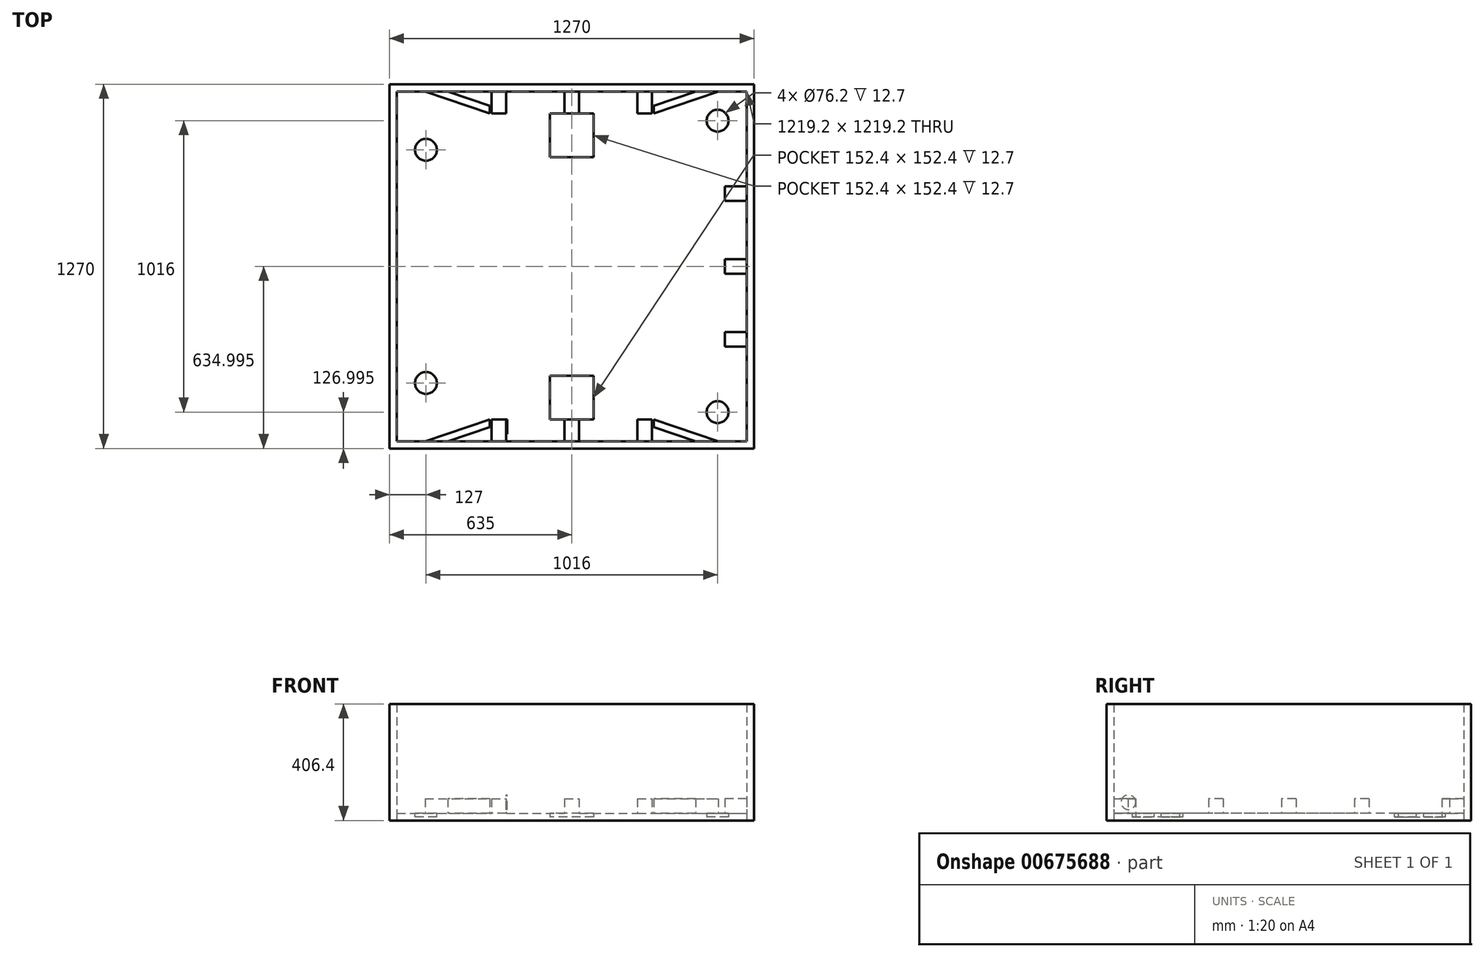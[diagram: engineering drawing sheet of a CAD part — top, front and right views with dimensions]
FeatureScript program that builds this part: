
annotation { "Feature Type Name" : "Feature", "Feature Type Description" : "" }
export const myFeature = defineFeature(function(context is Context, id is Id, definition is map)
    precondition{}
    {
        {
            var Q0;
            Q0=qCreatedBy(makeId("Top.planeOp"),FACE);
            var sketch = newSketch(context, id + "F0", { "sketchPlane" : qUnion([Q0])});
            skLineSegment(sketch, "E0.bottom", {"start": v(-620.85, 787.77) * mm, "end": v(598.35, 787.77) * mm});
            skLineSegment(sketch, "E0.top", {"start": v(-620.85, -431.43) * mm, "end": v(598.35, -431.43) * mm});
            skLineSegment(sketch, "E0.left", {"start": v(-620.85, 787.77) * mm, "end": v(-620.85, -431.43) * mm});
            skLineSegment(sketch, "E0.right", {"start": v(598.35, 787.77) * mm, "end": v(598.35, -431.43) * mm});
            skSolve(sketch);
        }
        {
            var Q0;
            Q0=makeQuery(id+"F0.imprint","IMPRINT",FACE,{"disambiguationData":[TD([[makeQuery(id+"F0.imprint","IMPRINT",EDGE,{"derivedFrom":sQuery(id+"F0.wireOp",EDGE,"E0.bottom")}),-1.0]])]});
            extrude(context, id + "F1", {"entities" : qUnion([Q0]), "depth" : 25.4 * mm, "offsetDistance" : 25.4 * mm});
        }
        {
            var Q0;
            Q0=makeQuery(id+"F1.opExtrude","CAP_FACE",FACE,{"disambiguationData":[OSD([sQuery(id+"F0.wireOp",EDGE,"E0.bottom"),sQuery(id+"F0.wireOp",EDGE,"E0.top"),sQuery(id+"F0.wireOp",EDGE,"E0.left"),sQuery(id+"F0.wireOp",EDGE,"E0.right")])],"isStart":false});
            var sketch = newSketch(context, id + "F2", { "sketchPlane" : qUnion([Q0])});
            skLineSegment(sketch, "E1", {"start": v(-36.65, -431.43) * mm, "end": v(-36.65, -355.23) * mm});
            skLineSegment(sketch, "E2", {"start": v(-36.65, -355.23) * mm, "end": v(14.15, -355.23) * mm});
            skLineSegment(sketch, "E3", {"start": v(14.15, -355.23) * mm, "end": v(14.15, -431.43) * mm});
            skLineSegment(sketch, "E4", {"start": v(14.15, -431.43) * mm, "end": v(-36.65, -431.43) * mm});
            skLineSegment(sketch, "E5.bottom", {"start": v(-239.85, -431.43) * mm, "end": v(-290.65, -431.43) * mm});
            skLineSegment(sketch, "E5.top", {"start": v(-239.85, -355.23) * mm, "end": v(-290.65, -355.23) * mm});
            skLineSegment(sketch, "E5.left", {"start": v(-239.85, -431.43) * mm, "end": v(-239.85, -355.23) * mm});
            skLineSegment(sketch, "E5.right", {"start": v(-290.65, -431.43) * mm, "end": v(-290.65, -355.23) * mm});
            skLineSegment(sketch, "E6.bottom", {"start": v(217.35, -431.43) * mm, "end": v(268.15, -431.43) * mm});
            skLineSegment(sketch, "E6.top", {"start": v(217.35, -355.23) * mm, "end": v(268.15, -355.23) * mm});
            skLineSegment(sketch, "E6.left", {"start": v(217.35, -431.43) * mm, "end": v(217.35, -355.23) * mm});
            skLineSegment(sketch, "E6.right", {"start": v(268.15, -431.43) * mm, "end": v(268.15, -355.23) * mm});
            skLineSegment(sketch, "E7.bottom", {"start": v(-239.85, 787.77) * mm, "end": v(-290.65, 787.77) * mm});
            skLineSegment(sketch, "E7.top", {"start": v(-239.85, 711.57) * mm, "end": v(-290.65, 711.57) * mm});
            skLineSegment(sketch, "E7.left", {"start": v(-239.85, 787.77) * mm, "end": v(-239.85, 711.57) * mm});
            skLineSegment(sketch, "E7.right", {"start": v(-290.65, 787.77) * mm, "end": v(-290.65, 711.57) * mm});
            skLineSegment(sketch, "E8.bottom", {"start": v(14.15, 787.77) * mm, "end": v(-36.65, 787.77) * mm});
            skLineSegment(sketch, "E8.top", {"start": v(14.15, 711.57) * mm, "end": v(-36.65, 711.57) * mm});
            skLineSegment(sketch, "E8.left", {"start": v(14.15, 787.77) * mm, "end": v(14.15, 711.57) * mm});
            skLineSegment(sketch, "E8.right", {"start": v(-36.65, 787.77) * mm, "end": v(-36.65, 711.57) * mm});
            skLineSegment(sketch, "E9.bottom", {"start": v(217.35, 787.77) * mm, "end": v(268.15, 787.77) * mm});
            skLineSegment(sketch, "E9.top", {"start": v(217.35, 711.57) * mm, "end": v(268.15, 711.57) * mm});
            skLineSegment(sketch, "E9.left", {"start": v(217.35, 787.77) * mm, "end": v(217.35, 711.57) * mm});
            skLineSegment(sketch, "E9.right", {"start": v(268.15, 787.77) * mm, "end": v(268.15, 711.57) * mm});
            skSolve(sketch);
        }
        {
            var Q0;
            Q0=makeQuery(id+"F2.imprint","IMPRINT",FACE,{"disambiguationData":[TD([[makeQuery(id+"F2.imprint","IMPRINT",EDGE,{"derivedFrom":sQuery(id+"F2.wireOp",EDGE,"E7.bottom")}),-1.0]])]});
            var Q1;
            Q1=makeQuery(id+"F2.imprint","IMPRINT",FACE,{"disambiguationData":[TD([[makeQuery(id+"F2.imprint","IMPRINT",EDGE,{"derivedFrom":sQuery(id+"F2.wireOp",EDGE,"E8.bottom")}),-1.0]])]});
            var Q2;
            Q2=makeQuery(id+"F2.imprint","IMPRINT",FACE,{"disambiguationData":[TD([[makeQuery(id+"F2.imprint","IMPRINT",EDGE,{"derivedFrom":sQuery(id+"F2.wireOp",EDGE,"E9.bottom")}),-1.0]])]});
            var Q3;
            Q3=makeQuery(id+"F2.imprint","IMPRINT",FACE,{"disambiguationData":[TD([[makeQuery(id+"F2.imprint","IMPRINT",EDGE,{"derivedFrom":sQuery(id+"F2.wireOp",EDGE,"E5.bottom")}),1.0]])]});
            var Q4;
            Q4=makeQuery(id+"F2.imprint","IMPRINT",FACE,{"disambiguationData":[TD([[makeQuery(id+"F2.imprint","IMPRINT",EDGE,{"derivedFrom":sQuery(id+"F2.wireOp",EDGE,"E1")}),-1.0]])]});
            var Q5;
            Q5=makeQuery(id+"F2.imprint","IMPRINT",FACE,{"disambiguationData":[TD([[makeQuery(id+"F2.imprint","IMPRINT",EDGE,{"derivedFrom":sQuery(id+"F2.wireOp",EDGE,"E6.bottom")}),1.0]])]});
            extrude(context, id + "F3", {"entities" : qUnion([Q0, Q1, Q2, Q3, Q4, Q5]), "operationType" : NewBodyOperationType.ADD, "depth" : 50.8 * mm, "offsetDistance" : 25.4 * mm});
        }
        {
            var Q0;
            Q0=makeQuery(id+"F1.opExtrude","CAP_FACE",FACE,{"disambiguationData":[OSD([sQuery(id+"F0.wireOp",EDGE,"E0.bottom"),sQuery(id+"F0.wireOp",EDGE,"E0.top"),sQuery(id+"F0.wireOp",EDGE,"E0.left"),sQuery(id+"F0.wireOp",EDGE,"E0.right")])],"isStart":false});
            var sketch = newSketch(context, id + "F4", { "sketchPlane" : qUnion([Q0])});
            skLineSegment(sketch, "E10", {"start": v(274.5, -355.23) * mm, "end": v(499.84, -431.43) * mm});
            skLineSegment(sketch, "E11", {"start": v(499.84, -431.43) * mm, "end": v(420.55, -431.43) * mm});
            skLineSegment(sketch, "E12", {"start": v(420.55, -431.43) * mm, "end": v(274.5, -382.05) * mm});
            skLineSegment(sketch, "E13", {"start": v(274.5, -382.05) * mm, "end": v(274.5, -355.23) * mm});
            skLineSegment(sketch, "E14", {"start": v(-522.34, -431.43) * mm, "end": v(-297, -355.23) * mm});
            skLineSegment(sketch, "E15", {"start": v(-297, -355.23) * mm, "end": v(-297, -382.05) * mm});
            skLineSegment(sketch, "E16", {"start": v(-297, -382.05) * mm, "end": v(-443.05, -431.43) * mm});
            skLineSegment(sketch, "E17", {"start": v(-443.05, -431.43) * mm, "end": v(-522.34, -431.43) * mm});
            skLineSegment(sketch, "E18", {"start": v(-522.34, 787.77) * mm, "end": v(-297, 711.57) * mm});
            skLineSegment(sketch, "E19", {"start": v(-297, 711.57) * mm, "end": v(-297, 738.38) * mm});
            skLineSegment(sketch, "E20", {"start": v(-297, 738.38) * mm, "end": v(-443.05, 787.77) * mm});
            skLineSegment(sketch, "E21", {"start": v(-443.05, 787.77) * mm, "end": v(-522.34, 787.77) * mm});
            skLineSegment(sketch, "E22", {"start": v(420.55, 787.77) * mm, "end": v(274.5, 738.38) * mm});
            skLineSegment(sketch, "E23", {"start": v(274.5, 738.38) * mm, "end": v(274.5, 711.57) * mm});
            skLineSegment(sketch, "E24", {"start": v(274.5, 711.57) * mm, "end": v(499.84, 787.77) * mm});
            skLineSegment(sketch, "E25", {"start": v(499.84, 787.77) * mm, "end": v(420.55, 787.77) * mm});
            skSolve(sketch);
        }
        {
            var Q0;
            Q0=makeQuery(id+"F4.imprint","IMPRINT",FACE,{"disambiguationData":[TD([[makeQuery(id+"F4.imprint","IMPRINT",EDGE,{"derivedFrom":sQuery(id+"F4.wireOp",EDGE,"E18")}),1.0]])]});
            var Q1;
            Q1=makeQuery(id+"F4.imprint","IMPRINT",FACE,{"disambiguationData":[TD([[makeQuery(id+"F4.imprint","IMPRINT",EDGE,{"derivedFrom":sQuery(id+"F4.wireOp",EDGE,"E22")}),1.0]])]});
            var Q2;
            Q2=makeQuery(id+"F4.imprint","IMPRINT",FACE,{"disambiguationData":[TD([[makeQuery(id+"F4.imprint","IMPRINT",EDGE,{"derivedFrom":sQuery(id+"F4.wireOp",EDGE,"E10")}),-1.0]])]});
            var Q3;
            Q3=makeQuery(id+"F4.imprint","IMPRINT",FACE,{"disambiguationData":[TD([[makeQuery(id+"F4.imprint","IMPRINT",EDGE,{"derivedFrom":sQuery(id+"F4.wireOp",EDGE,"E14")}),-1.0]])]});
            extrude(context, id + "F5", {"entities" : qUnion([Q0, Q1, Q2, Q3]), "depth" : 50.8 * mm, "offsetDistance" : 25.4 * mm});
        }
        {
            var Q0;
            Q0=makeQuery(id+"F1.opExtrude","CAP_FACE",FACE,{"disambiguationData":[OSD([sQuery(id+"F0.wireOp",EDGE,"E0.bottom"),sQuery(id+"F0.wireOp",EDGE,"E0.top"),sQuery(id+"F0.wireOp",EDGE,"E0.left"),sQuery(id+"F0.wireOp",EDGE,"E0.right")])],"isStart":false});
            var sketch = newSketch(context, id + "F6", { "sketchPlane" : qUnion([Q0])});
            skLineSegment(sketch, "E26.bottom", {"start": v(598.35, 203.57) * mm, "end": v(522.15, 203.57) * mm});
            skLineSegment(sketch, "E26.top", {"start": v(598.35, 152.77) * mm, "end": v(522.15, 152.77) * mm});
            skLineSegment(sketch, "E26.left", {"start": v(598.35, 203.57) * mm, "end": v(598.35, 152.77) * mm});
            skLineSegment(sketch, "E26.right", {"start": v(522.15, 203.57) * mm, "end": v(522.15, 152.77) * mm});
            skLineSegment(sketch, "E27.bottom", {"start": v(598.35, 457.57) * mm, "end": v(522.15, 457.57) * mm});
            skLineSegment(sketch, "E27.top", {"start": v(598.35, 406.77) * mm, "end": v(522.15, 406.77) * mm});
            skLineSegment(sketch, "E27.left", {"start": v(598.35, 457.57) * mm, "end": v(598.35, 406.77) * mm});
            skLineSegment(sketch, "E27.right", {"start": v(522.15, 457.57) * mm, "end": v(522.15, 406.77) * mm});
            skLineSegment(sketch, "E28.bottom", {"start": v(522.15, -50.43) * mm, "end": v(598.35, -50.43) * mm});
            skLineSegment(sketch, "E28.top", {"start": v(522.15, -101.23) * mm, "end": v(598.35, -101.23) * mm});
            skLineSegment(sketch, "E28.left", {"start": v(522.15, -50.43) * mm, "end": v(522.15, -101.23) * mm});
            skLineSegment(sketch, "E28.right", {"start": v(598.35, -50.43) * mm, "end": v(598.35, -101.23) * mm});
            skSolve(sketch);
        }
        {
            var Q0;
            Q0=makeQuery(id+"F6.imprint","IMPRINT",FACE,{"disambiguationData":[TD([[makeQuery(id+"F6.imprint","IMPRINT",EDGE,{"derivedFrom":sQuery(id+"F6.wireOp",EDGE,"E27.bottom")}),1.0]])]});
            var Q1;
            Q1=makeQuery(id+"F6.imprint","IMPRINT",FACE,{"disambiguationData":[TD([[makeQuery(id+"F6.imprint","IMPRINT",EDGE,{"derivedFrom":sQuery(id+"F6.wireOp",EDGE,"E26.bottom")}),1.0]])]});
            var Q2;
            Q2=makeQuery(id+"F6.imprint","IMPRINT",FACE,{"disambiguationData":[TD([[makeQuery(id+"F6.imprint","IMPRINT",EDGE,{"derivedFrom":sQuery(id+"F6.wireOp",EDGE,"E28.bottom")}),-1.0]])]});
            extrude(context, id + "F7", {"entities" : qUnion([Q0, Q1, Q2]), "operationType" : NewBodyOperationType.ADD, "depth" : 50.8 * mm, "offsetDistance" : 25.4 * mm});
        }
        {
            var Q0;
            Q0=makeQuery(id+"F1.opExtrude","CAP_FACE",FACE,{"disambiguationData":[OSD([sQuery(id+"F0.wireOp",EDGE,"E0.bottom"),sQuery(id+"F0.wireOp",EDGE,"E0.top"),sQuery(id+"F0.wireOp",EDGE,"E0.left"),sQuery(id+"F0.wireOp",EDGE,"E0.right")])],"isStart":true});
            var sketch = newSketch(context, id + "F8", { "sketchPlane" : qUnion([Q0])});
            skLineSegment(sketch, "E29", {"start": v(-620.85, 431.43) * mm, "end": v(-620.85, -787.77) * mm});
            skLineSegment(sketch, "E30", {"start": v(-620.85, -787.77) * mm, "end": v(598.35, -787.77) * mm});
            skLineSegment(sketch, "E31", {"start": v(598.35, -787.77) * mm, "end": v(598.35, 431.43) * mm});
            skLineSegment(sketch, "E32", {"start": v(598.35, 431.43) * mm, "end": v(-620.85, 431.43) * mm});
            skLineSegment(sketch, "E33", {"start": v(-671.65, 482.23) * mm, "end": v(-671.65, -838.57) * mm});
            skLineSegment(sketch, "E34", {"start": v(-671.65, -838.57) * mm, "end": v(649.15, -838.57) * mm});
            skLineSegment(sketch, "E35", {"start": v(649.15, -838.57) * mm, "end": v(649.15, 482.23) * mm});
            skLineSegment(sketch, "E36", {"start": v(649.15, 482.23) * mm, "end": v(-671.65, 482.23) * mm});
            skSolve(sketch);
        }
        {
            var Q0;
            Q0=makeQuery(id+"F8.imprint","IMPRINT",FACE,{"disambiguationData":[TD([[makeQuery(id+"F8.imprint","IMPRINT",EDGE,{"derivedFrom":sQuery(id+"F8.wireOp",EDGE,"E29")}),1.0]])]});
            extrude(context, id + "F9", {"entities" : qUnion([Q0]), "oppositeDirection" : true, "depth" : 609.6 * mm, "offsetDistance" : 25.4 * mm});
        }
        {
            var Q0;
            Q0=makeQuery(id+"F9.opExtrude","SWEPT_FACE",FACE,{"disambiguationData":[OSD([sQuery(id+"F8.wireOp",EDGE,"E34")])]});
            extrude(context, id + "F10", {"entities" : qUnion([Q0]), "operationType" : NewBodyOperationType.REMOVE, "oppositeDirection" : true, "depth" : 25.4 * mm, "offsetDistance" : 25.4 * mm});
        }
        {
            var Q0;
            Q0=makeQuery(id+"F9.opExtrude","SWEPT_FACE",FACE,{"disambiguationData":[OSD([sQuery(id+"F8.wireOp",EDGE,"E33")])]});
            extrude(context, id + "F11", {"entities" : qUnion([Q0]), "operationType" : NewBodyOperationType.REMOVE, "oppositeDirection" : true, "depth" : 25.4 * mm, "offsetDistance" : 25.4 * mm});
        }
        {
            var Q0;
            Q0=makeQuery(id+"F9.opExtrude","SWEPT_FACE",FACE,{"disambiguationData":[OSD([sQuery(id+"F8.wireOp",EDGE,"E36")])]});
            extrude(context, id + "F12", {"entities" : qUnion([Q0]), "operationType" : NewBodyOperationType.REMOVE, "oppositeDirection" : true, "depth" : 25.4 * mm, "offsetDistance" : 25.4 * mm});
        }
        {
            var Q0;
            Q0=makeQuery(id+"F9.opExtrude","SWEPT_FACE",FACE,{"disambiguationData":[OSD([sQuery(id+"F8.wireOp",EDGE,"E35")])]});
            extrude(context, id + "F13", {"entities" : qUnion([Q0]), "operationType" : NewBodyOperationType.REMOVE, "oppositeDirection" : true, "depth" : 25.4 * mm, "offsetDistance" : 25.4 * mm});
        }
        {
            var Q0;
            Q0=makeQuery(id+"F9.opExtrude","CAP_FACE",FACE,{"disambiguationData":[OSD([sQuery(id+"F8.wireOp",EDGE,"E29"),sQuery(id+"F8.wireOp",EDGE,"E30"),sQuery(id+"F8.wireOp",EDGE,"E31"),sQuery(id+"F8.wireOp",EDGE,"E32"),sQuery(id+"F8.wireOp",EDGE,"E33"),sQuery(id+"F8.wireOp",EDGE,"E34"),sQuery(id+"F8.wireOp",EDGE,"E35"),sQuery(id+"F8.wireOp",EDGE,"E36")])],"isStart":false});
            extrude(context, id + "F14", {"entities" : qUnion([Q0]), "operationType" : NewBodyOperationType.REMOVE, "oppositeDirection" : true, "depth" : 203.2 * mm, "offsetDistance" : 25.4 * mm});
        }
        {
            var Q0;
            Q0=makeQuery(id+"F1.opExtrude","CAP_FACE",FACE,{"disambiguationData":[OSD([sQuery(id+"F0.wireOp",EDGE,"E0.bottom"),sQuery(id+"F0.wireOp",EDGE,"E0.top"),sQuery(id+"F0.wireOp",EDGE,"E0.left"),sQuery(id+"F0.wireOp",EDGE,"E0.right")])],"isStart":false});
            var sketch = newSketch(context, id + "F15", { "sketchPlane" : qUnion([Q0])});
            skLineSegment(sketch, "E37.bottom", {"start": v(64.95, -202.83) * mm, "end": v(-87.45, -202.83) * mm});
            skLineSegment(sketch, "E37.top", {"start": v(64.95, -355.23) * mm, "end": v(-87.45, -355.23) * mm});
            skLineSegment(sketch, "E37.left", {"start": v(64.95, -202.83) * mm, "end": v(64.95, -355.23) * mm});
            skLineSegment(sketch, "E37.right", {"start": v(-87.45, -202.83) * mm, "end": v(-87.45, -355.23) * mm});
            skPoint(sketch, "E37.middle", {"position": v(-11.25, -279.03) * mm});
            skPoint(sketch, "E37.middle.positionSnap0", {"position": v(-11.25, -355.23) * mm});
            skPoint(sketch, "E37.centerSnap0", {"position": v(-11.25, -355.23) * mm});
            skLineSegment(sketch, "E38.bottom", {"start": v(64.95, 559.17) * mm, "end": v(-87.45, 559.17) * mm});
            skLineSegment(sketch, "E38.top", {"start": v(64.95, 711.57) * mm, "end": v(-87.45, 711.57) * mm});
            skLineSegment(sketch, "E38.left", {"start": v(64.95, 559.17) * mm, "end": v(64.95, 711.57) * mm});
            skLineSegment(sketch, "E38.right", {"start": v(-87.45, 559.17) * mm, "end": v(-87.45, 711.57) * mm});
            skPoint(sketch, "E38.middle", {"position": v(-11.25, 635.37) * mm});
            skPoint(sketch, "E38.middle.positionSnap0", {"position": v(-11.25, 711.57) * mm});
            skPoint(sketch, "E38.centerSnap0", {"position": v(-11.25, 711.57) * mm});
            skSolve(sketch);
        }
        {
            var Q0;
            Q0=makeQuery(id+"F15.imprint","IMPRINT",FACE,{"disambiguationData":[TD([[makeQuery(id+"F15.imprint","IMPRINT",EDGE,{"derivedFrom":sQuery(id+"F15.wireOp",EDGE,"E38.bottom")}),-1.0]])]});
            var Q1;
            Q1=makeQuery(id+"F15.imprint","IMPRINT",FACE,{"disambiguationData":[TD([[makeQuery(id+"F15.imprint","IMPRINT",EDGE,{"derivedFrom":sQuery(id+"F15.wireOp",EDGE,"E37.bottom")}),1.0]])]});
            extrude(context, id + "F16", {"entities" : qUnion([Q0, Q1]), "operationType" : NewBodyOperationType.REMOVE, "oppositeDirection" : true, "depth" : 12.7 * mm, "offsetDistance" : 25.4 * mm});
        }
        {
            var Q0;
            Q0=makeQuery(id+"F16.boolean.opBoolean","COPY",FACE,{"derivedFrom":makeQuery(id+"F16.opExtrude","CAP_FACE",FACE,{"disambiguationData":[OSD([sQuery(id+"F15.wireOp",EDGE,"E38.bottom"),sQuery(id+"F15.wireOp",EDGE,"E38.top"),sQuery(id+"F15.wireOp",EDGE,"E38.left"),sQuery(id+"F15.wireOp",EDGE,"E38.right")])],"isStart":false})});
            var Q1;
            Q1=makeQuery(id+"F16.boolean.opBoolean","COPY",FACE,{"derivedFrom":makeQuery(id+"F16.opExtrude","CAP_FACE",FACE,{"disambiguationData":[OSD([sQuery(id+"F15.wireOp",EDGE,"E37.bottom"),sQuery(id+"F15.wireOp",EDGE,"E37.top"),sQuery(id+"F15.wireOp",EDGE,"E37.left"),sQuery(id+"F15.wireOp",EDGE,"E37.right")])],"isStart":false})});
            extrude(context, id + "F17", {"entities" : qUnion([Q0, Q1]), "depth" : 12.7 * mm, "offsetDistance" : 25.4 * mm});
        }
        {
            var Q0;
            Q0=makeQuery(id+"F1.opExtrude","CAP_FACE",FACE,{"disambiguationData":[OSD([sQuery(id+"F0.wireOp",EDGE,"E0.bottom"),sQuery(id+"F0.wireOp",EDGE,"E0.top"),sQuery(id+"F0.wireOp",EDGE,"E0.left"),sQuery(id+"F0.wireOp",EDGE,"E0.right")])],"isStart":false});
            var sketch = newSketch(context, id + "F18", { "sketchPlane" : qUnion([Q0])});
            skCircle(sketch, "E39", {"center": v(496.75, 686.17) * mm, "radius": 38.1 * mm});
            skCircle(sketch, "E40", {"center": v(496.75, -329.83) * mm, "radius": 38.1 * mm});
            skCircle(sketch, "E41", {"center": v(-519.25, -228.23) * mm, "radius": 38.1 * mm});
            skCircle(sketch, "E42", {"center": v(-519.25, 584.57) * mm, "radius": 38.1 * mm});
            skSolve(sketch);
        }
        {
            var Q0;
            Q0=makeQuery(id+"F18.imprint","IMPRINT",FACE,{"disambiguationData":[TD([[makeQuery(id+"F18.imprint","IMPRINT",EDGE,{"derivedFrom":sQuery(id+"F18.wireOp",EDGE,"E42")}),1.0]])]});
            var Q1;
            Q1=makeQuery(id+"F18.imprint","IMPRINT",FACE,{"disambiguationData":[TD([[makeQuery(id+"F18.imprint","IMPRINT",EDGE,{"derivedFrom":sQuery(id+"F18.wireOp",EDGE,"E41")}),1.0]])]});
            var Q2;
            Q2=makeQuery(id+"F18.imprint","IMPRINT",FACE,{"disambiguationData":[TD([[makeQuery(id+"F18.imprint","IMPRINT",EDGE,{"derivedFrom":sQuery(id+"F18.wireOp",EDGE,"E40")}),1.0]])]});
            var Q3;
            Q3=makeQuery(id+"F18.imprint","IMPRINT",FACE,{"disambiguationData":[TD([[makeQuery(id+"F18.imprint","IMPRINT",EDGE,{"derivedFrom":sQuery(id+"F18.wireOp",EDGE,"E39")}),1.0]])]});
            extrude(context, id + "F19", {"entities" : qUnion([Q0, Q1, Q2, Q3]), "operationType" : NewBodyOperationType.REMOVE, "oppositeDirection" : true, "depth" : 12.7 * mm, "offsetDistance" : 25.4 * mm});
        }
        {
            var Q0;
            Q0=makeQuery(id+"F19.boolean.opBoolean","COPY",FACE,{"derivedFrom":makeQuery(id+"F19.opExtrude","CAP_FACE",FACE,{"disambiguationData":[OSD([sQuery(id+"F18.wireOp",EDGE,"E41")])],"isStart":false})});
            var Q1;
            Q1=makeQuery(id+"F19.boolean.opBoolean","COPY",FACE,{"derivedFrom":makeQuery(id+"F19.opExtrude","CAP_FACE",FACE,{"disambiguationData":[OSD([sQuery(id+"F18.wireOp",EDGE,"E42")])],"isStart":false})});
            var Q2;
            Q2=makeQuery(id+"F19.boolean.opBoolean","COPY",FACE,{"derivedFrom":makeQuery(id+"F19.opExtrude","CAP_FACE",FACE,{"disambiguationData":[OSD([sQuery(id+"F18.wireOp",EDGE,"E39")])],"isStart":false})});
            var Q3;
            Q3=makeQuery(id+"F19.boolean.opBoolean","COPY",FACE,{"derivedFrom":makeQuery(id+"F19.opExtrude","CAP_FACE",FACE,{"disambiguationData":[OSD([sQuery(id+"F18.wireOp",EDGE,"E40")])],"isStart":false})});
            extrude(context, id + "F20", {"entities" : qUnion([Q0, Q1, Q2, Q3]), "depth" : 12.7 * mm, "offsetDistance" : 25.4 * mm});
        }
        {
            var Q0;
            Q0=makeQuery(id+"F3.opExtrude","SWEPT_FACE",FACE,{"disambiguationData":[OSD([sQuery(id+"F2.wireOp",EDGE,"E5.left")])]});
            var sketch = newSketch(context, id + "F21", { "sketchPlane" : qUnion([Q0])});
            skCircle(sketch, "E43", {"center": v(-380.63, 63.5) * mm, "radius": 25.4 * mm});
            skPoint(sketch, "E43.centerSnap0", {"position": v(-353.43, 63.5) * mm});
            skSolve(sketch);
        }
        {
            var Q0;
            {var subQ0=sQuery(id+"F21.wireOp",EDGE,"E43");var subQ1=sQuery(id+"F2.wireOp",EDGE,"E5.left");var subQ2=makeQuery(id+"F3.opExtrude","CAP_EDGE",EDGE,{"disambiguationData":[OSD([subQ1])],"isStart":false});var subQ3=makeQuery(id+"F21.imprint","INTERSECT",VERTEX,{"disambiguationData":[OD(0.0)],"derivedFrom":[subQ2,subQ0]});Q0=makeQuery(id+"F21.imprint","IMPRINT",FACE,{"disambiguationData":[TD([[makeQuery(id+"F21.imprint","IMPRINT",EDGE,{"disambiguationData":[TD([[subQ3,1.0]])],"derivedFrom":subQ2}),-1.0]])]});}
            var Q1;
            {var subQ0=sQuery(id+"F21.wireOp",EDGE,"E43");var subQ1=makeQuery(id+"F3.opExtrude","CAP_EDGE",EDGE,{"disambiguationData":[OSD([sQuery(id+"F2.wireOp",EDGE,"E5.left")])],"isStart":false});var subQ2=makeQuery(id+"F21.imprint","INTERSECT",VERTEX,{"disambiguationData":[OD(0.0)],"derivedFrom":[subQ1,subQ0]});Q1=makeQuery(id+"F21.imprint","IMPRINT",FACE,{"disambiguationData":[TD([[makeQuery(id+"F21.imprint","IMPRINT",EDGE,{"disambiguationData":[TD([[subQ2,-1.0]])],"derivedFrom":subQ0}),1.0]])]});}
            extrude(context, id + "F22", {"entities" : qUnion([Q0, Q1]), "depth" : 3.2 * mm, "offsetDistance" : 25.4 * mm});
        }
    });
